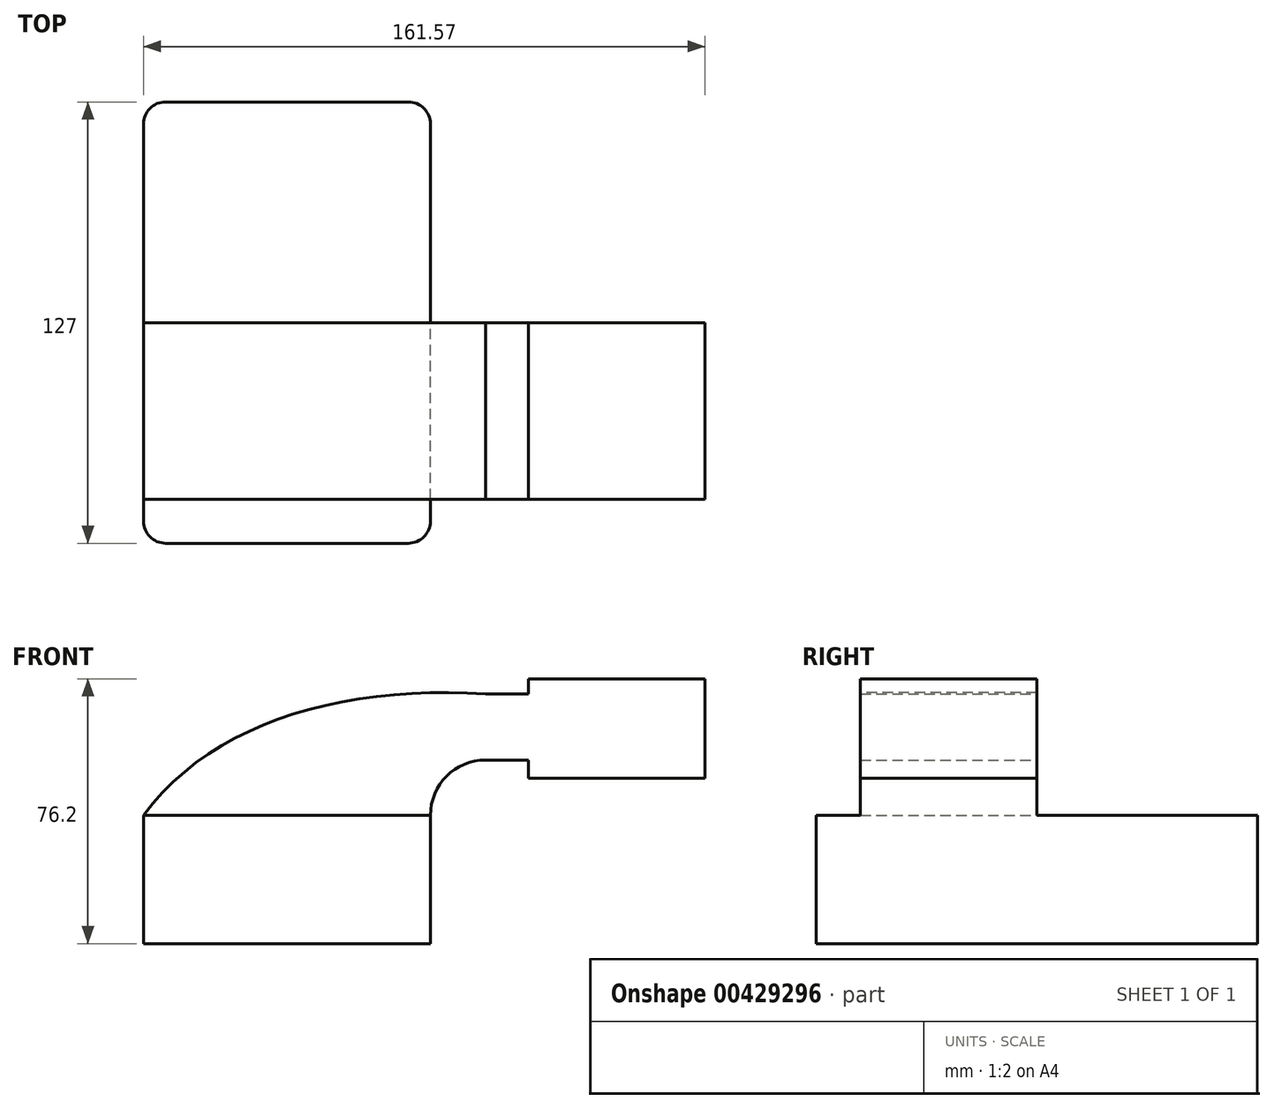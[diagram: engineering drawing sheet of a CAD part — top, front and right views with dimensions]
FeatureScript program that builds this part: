
annotation { "Feature Type Name" : "Feature", "Feature Type Description" : "" }
export const myFeature = defineFeature(function(context is Context, id is Id, definition is map)
    precondition{}
    {
        {
            var Q0;
            Q0=qCreatedBy(makeId("Front.planeOp"),FACE);
            var sketch = newSketch(context, id + "F0", { "sketchPlane" : qUnion([Q0])});
            skLineSegment(sketch, "E0.bottom", {"start": v(-41.27, 18.46) * mm, "end": v(41.27, 18.46) * mm});
            skLineSegment(sketch, "E0.top", {"start": v(-41.27, -18.46) * mm, "end": v(41.27, -18.46) * mm});
            skLineSegment(sketch, "E0.left", {"start": v(-41.28, 18.46) * mm, "end": v(-41.28, -18.46) * mm});
            skLineSegment(sketch, "E0.right", {"start": v(41.28, 18.46) * mm, "end": v(41.28, -18.46) * mm});
            skPoint(sketch, "E0.middle", {"position": v(0, 0) * mm});
            skLineSegment(sketch, "E1", {"start": v(41.27, 18.46) * mm, "end": v(41.27, 18.46) * mm});
            skArc(sketch, "E2", {"start": v(41.27, 18.46) * mm, "mid": v(45.92, 29.69) * mm, "end": v(57.15, 34.34) * mm});
            skLineSegment(sketch, "E3", {"start": v(57.15, 34.34) * mm, "end": v(82.55, 34.34) * mm});
            skLineSegment(sketch, "E4.bottom", {"start": v(69.5, 57.74) * mm, "end": v(120.3, 57.74) * mm});
            skLineSegment(sketch, "E4.top", {"start": v(69.5, 29.16) * mm, "end": v(120.3, 29.16) * mm});
            skLineSegment(sketch, "E4.left", {"start": v(69.5, 57.74) * mm, "end": v(69.5, 29.16) * mm});
            skLineSegment(sketch, "E4.right", {"start": v(120.3, 57.74) * mm, "end": v(120.3, 29.16) * mm});
            skPoint(sketch, "E4.middle", {"position": v(94.9, 43.45) * mm});
            skLineSegment(sketch, "E5.0", {"start": v(57.15, 53.39) * mm, "end": v(82.55, 53.39) * mm});
            skArc(sketch, "E5.1", {"start": v(22.22, 18.46) * mm, "mid": v(32.45, 43.16) * mm, "end": v(57.15, 53.39) * mm});
            skLineSegment(sketch, "E5.2", {"start": v(22.23, 18.46) * mm, "end": v(22.23, 18.46) * mm});
            skLineSegment(sketch, "E6.0", {"start": v(57.15, 53) * mm, "end": v(82.55, 53) * mm});
            skFitSpline(sketch, "E7", {"points": [v(-41.27, 18.46) * mm, v(57.15, 53.39) * mm], "startDerivative": vector(58.75, 80) * mm, "endDerivative": vector(124.48, -7.65) * mm});
            skSolve(sketch);
        }
        {
            var Q0;
            Q0=makeQuery(id+"F0.imprint","IMPRINT",FACE,{"disambiguationData":[TD([[makeQuery(id+"F0.imprint","IMPRINT",EDGE,{"derivedFrom":sQuery(id+"F0.wireOp",EDGE,"E0.top")}),1.0]])]});
            extrude(context, id + "F1", {"entities" : qUnion([Q0]), "endBound" : BoundingType.SYMMETRIC, "depth" : 127 * mm});
        }
        {
            var Q0;
            Q0 = qSketchRegion(id + "F0", true);
            extrude(context, id + "F2", {"entities" : qUnion([Q0]), "operationType" : NewBodyOperationType.ADD, "depth" : 50.8 * mm});
        }
        {
            var Q0;
            Q0 = qSketchRegion(id + "F0", true);
            extrude(context, id + "F3", {"entities" : qUnion([Q0]), "operationType" : NewBodyOperationType.ADD, "depth" : 15.88 * mm});
        }
        {
            var Q0;
            Q0=makeQuery(id+"F1.opExtrude","CAP_EDGE",EDGE,{"disambiguationData":[OSD([sQuery(id+"F0.wireOp",EDGE,"E0.right")])],"isStart":false});
            var Q1;
            Q1=makeQuery(id+"F1.opExtrude","CAP_EDGE",EDGE,{"disambiguationData":[OSD([sQuery(id+"F0.wireOp",EDGE,"E0.left")])],"isStart":false});
            var Q2;
            Q2=makeQuery(id+"F1.opExtrude","CAP_EDGE",EDGE,{"disambiguationData":[OSD([sQuery(id+"F0.wireOp",EDGE,"E0.right")])],"isStart":true});
            var Q3;
            Q3=makeQuery(id+"F1.opExtrude","CAP_EDGE",EDGE,{"disambiguationData":[OSD([sQuery(id+"F0.wireOp",EDGE,"E0.left")])],"isStart":true});
            fillet(context, id + "F4", {"entities" : qUnion([Q0, Q1, Q2, Q3]), "radius" : 6.35 * mm, "tangentPropagation" : true, "allowEdgeOverflow" : false});
        }
    });
